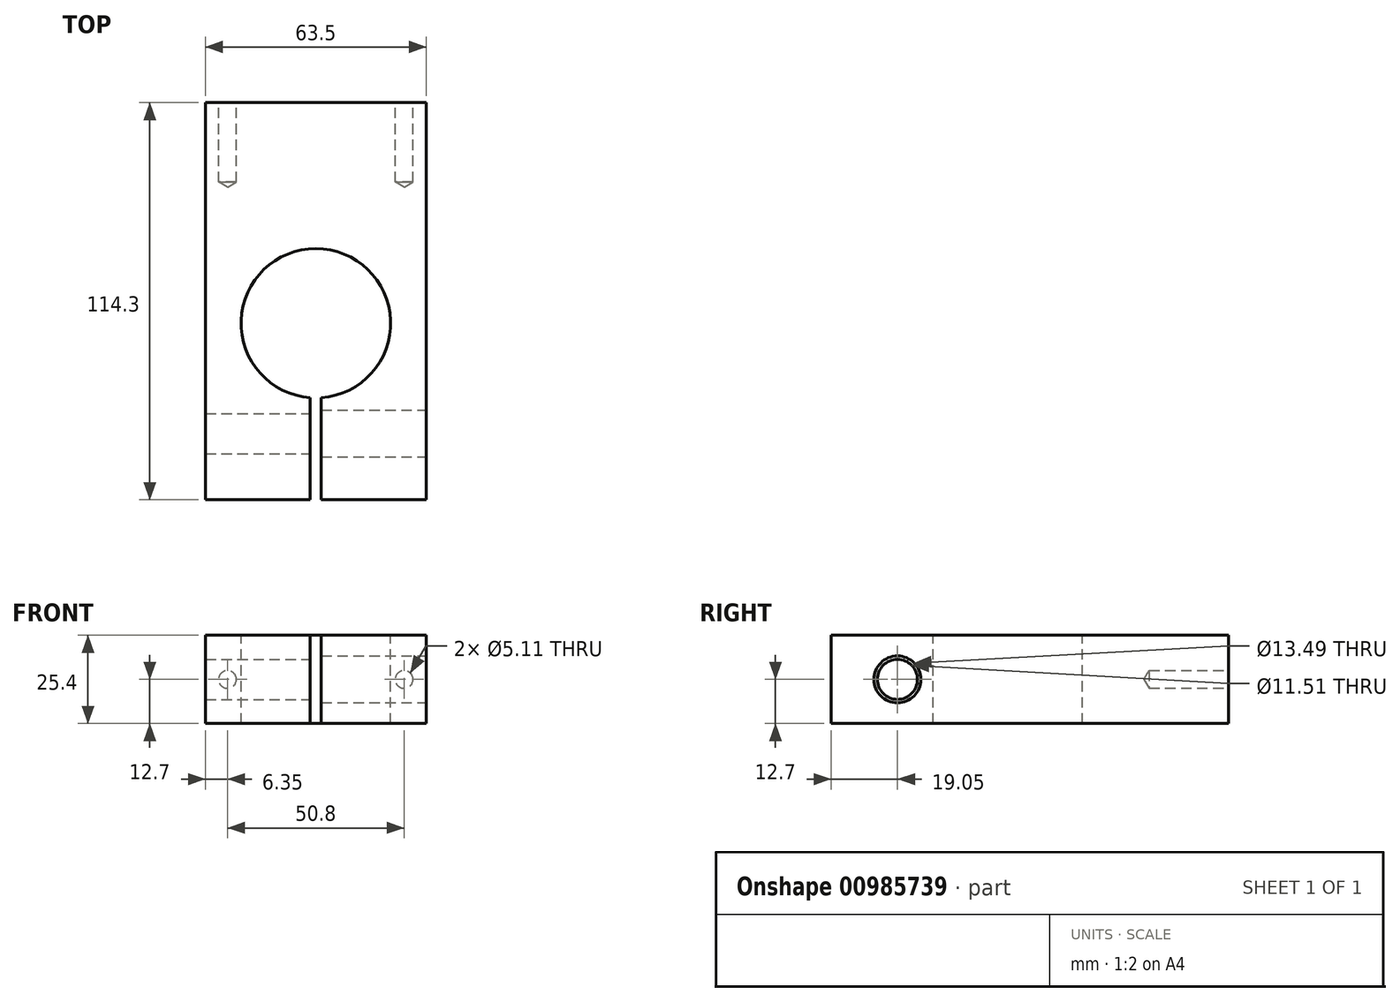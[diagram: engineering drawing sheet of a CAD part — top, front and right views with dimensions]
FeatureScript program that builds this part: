
annotation { "Feature Type Name" : "Feature", "Feature Type Description" : "" }
export const myFeature = defineFeature(function(context is Context, id is Id, definition is map)
    precondition{}
    {
        {
            var Q0;
            Q0=qCreatedBy(makeId("Top.planeOp"),FACE);
            var sketch = newSketch(context, id + "F0", { "sketchPlane" : qUnion([Q0])});
            skLineSegment(sketch, "E0.bottom", {"start": v(0, 0) * mm, "end": v(63.5, 0) * mm});
            skLineSegment(sketch, "E0.top", {"start": v(0, -114.3) * mm, "end": v(63.5, -114.3) * mm});
            skLineSegment(sketch, "E0.left", {"start": v(0, 0) * mm, "end": v(0, -114.3) * mm});
            skLineSegment(sketch, "E0.right", {"start": v(63.5, 0) * mm, "end": v(63.5, -114.3) * mm});
            skSolve(sketch);
        }
        {
            var Q0;
            Q0 = qSketchRegion(id + "F0", true);
            extrude(context, id + "F1", {"entities" : qUnion([Q0]), "depth" : 25.4 * mm, "offsetDistance" : 25.4 * mm});
        }
        {
            var Q0;
            Q0=makeQuery(id+"F1.opExtrude","SWEPT_FACE",FACE,{"disambiguationData":[OSD([sQuery(id+"F0.wireOp",EDGE,"E0.bottom")])]});
            var sketch = newSketch(context, id + "F2", { "sketchPlane" : qUnion([Q0])});
            skLineSegment(sketch, "E1", {"start": v(-57.15, 12.7) * mm, "end": v(-6.35, 12.7) * mm, "construction": true});
            skLineSegment(sketch, "E2", {"start": v(-57.15, 12.7) * mm, "end": v(-63.5, 12.7) * mm, "construction": true});
            skLineSegment(sketch, "E3", {"start": v(-31.75, 12.7) * mm, "end": v(-31.75, 25.4) * mm, "construction": true});
            skSolve(sketch);
        }
        {
            var Q0;
            Q0=sQuery(id+"F2.wireOp",VERTEX,"E1.start");
            var Q1;
            Q1=sQuery(id+"F2.wireOp",VERTEX,"E1.end");
            var Q2;
            Q2=makeQuery(id+"F1.opExtrude","SWEPT_BODY",BODY,{"disambiguationData":[OSD([sQuery(id+"F0.wireOp",EDGE,"E0.bottom"),sQuery(id+"F0.wireOp",EDGE,"E0.top"),sQuery(id+"F0.wireOp",EDGE,"E0.left"),sQuery(id+"F0.wireOp",EDGE,"E0.right")])]});
            hole(context, id + "F3", {"style" : HoleStyle.SIMPLE, "endStyle" : HoleEndStyle.BLIND, "standardTappedOrClearance" : lookupTablePath({ "standard" : "ANSI", "engagement" : "75%", "pitch" : "20 tpi", "size" : "1/4", "type" : "Tapped" }), "standardBlindInLast" : lookupTablePath({ "standard" : "ANSI", "fit" : "Free", "engagement" : "75%", "pitch" : "20 tpi", "size" : "1/4", "type" : "Clearance & tapped" }), "holeDiameter" : 5.1 * mm, "majorDiameter" : 6.35 * mm, "showTappedDepth" : true, "holeDepth" : 22.86 * mm, "isTappedThrough" : true, "tappedDepth" : 19.05 * mm, "tapClearance" : 3, "startFromSketch" : true, "locations" : qUnion([Q0, Q1]), "scope" : qUnion([Q2])});
        }
        {
            var Q0;
            Q0=makeQuery(id+"F1.opExtrude","CAP_FACE",FACE,{"disambiguationData":[OSD([sQuery(id+"F0.wireOp",EDGE,"E0.bottom"),sQuery(id+"F0.wireOp",EDGE,"E0.top"),sQuery(id+"F0.wireOp",EDGE,"E0.left"),sQuery(id+"F0.wireOp",EDGE,"E0.right")])],"isStart":false});
            var sketch = newSketch(context, id + "F4", { "sketchPlane" : qUnion([Q0])});
            skArc(sketch, "E4", {"start": v(33.34, -84.94) * mm, "mid": v(31.75, -42) * mm, "end": v(30.16, -84.94) * mm});
            skPoint(sketch, "E4.centerSnap0", {"position": v(31.75, -114.3) * mm});
            skLineSegment(sketch, "E5", {"start": v(31.75, -63.5) * mm, "end": v(31.75, 0) * mm, "construction": true});
            skLineSegment(sketch, "E6.top", {"start": v(30.16, -114.3) * mm, "end": v(33.34, -114.3) * mm});
            skLineSegment(sketch, "E6.left", {"start": v(30.16, -84.94) * mm, "end": v(30.16, -114.3) * mm});
            skLineSegment(sketch, "E6.right", {"start": v(33.34, -84.94) * mm, "end": v(33.34, -114.3) * mm});
            skLineSegment(sketch, "E7", {"start": v(30.16, -84.94) * mm, "end": v(33.34, -84.94) * mm, "construction": true});
            skSolve(sketch);
        }
        {
            var Q0;
            Q0 = qSketchRegion(id + "F4", true);
            extrude(context, id + "F5", {"entities" : qUnion([Q0]), "operationType" : NewBodyOperationType.REMOVE, "endBound" : BoundingType.UP_TO_NEXT, "oppositeDirection" : true, "depth" : 25.4 * mm, "offsetDistance" : 25.4 * mm});
        }
        {
            var Q0;
            Q0=makeQuery(id+"F1.opExtrude","SWEPT_FACE",FACE,{"disambiguationData":[OSD([sQuery(id+"F0.wireOp",EDGE,"E0.right")])]});
            var sketch = newSketch(context, id + "F6", { "sketchPlane" : qUnion([Q0])});
            skLineSegment(sketch, "E8", {"start": v(-114.3, 12.7) * mm, "end": v(-95.25, 12.7) * mm, "construction": true});
            skLineSegment(sketch, "E9", {"start": v(-63.5, 25.4) * mm, "end": v(-63.5, 0) * mm, "construction": true});
            skCircle(sketch, "E10", {"center": v(-95.25, 12.7) * mm, "radius": 6.75 * mm});
            skSolve(sketch);
        }
        {
            var Q0;
            Q0 = qSketchRegion(id + "F6", true);
            extrude(context, id + "F7", {"entities" : qUnion([Q0]), "operationType" : NewBodyOperationType.REMOVE, "endBound" : BoundingType.UP_TO_NEXT, "oppositeDirection" : true, "depth" : 25.4 * mm, "offsetDistance" : 25.4 * mm});
        }
        {
            var Q0;
            Q0=makeQuery(id+"F5.boolean.opBoolean","COPY",FACE,{"derivedFrom":makeQuery(id+"F5.opExtrude","SWEPT_FACE",FACE,{"disambiguationData":[OSD([sQuery(id+"F4.wireOp",EDGE,"E6.left")])]})});
            var sketch = newSketch(context, id + "F8", { "sketchPlane" : qUnion([Q0])});
            skCircle(sketch, "E11.0", {"center": v(-95.25, 12.7) * mm, "radius": 6.75 * mm});
            skSolve(sketch);
        }
        {
            var Q0;
            Q0=sQuery(id+"F8.wireOp",VERTEX,"E11.0.center");
            var Q1;
            Q1=makeQuery(id+"F1.opExtrude","SWEPT_BODY",BODY,{"disambiguationData":[OSD([sQuery(id+"F0.wireOp",EDGE,"E0.bottom"),sQuery(id+"F0.wireOp",EDGE,"E0.top"),sQuery(id+"F0.wireOp",EDGE,"E0.left"),sQuery(id+"F0.wireOp",EDGE,"E0.right")])]});
            hole(context, id + "F9", {"style" : HoleStyle.SIMPLE, "endStyle" : HoleEndStyle.THROUGH, "standardTappedOrClearance" : lookupTablePath({ "standard" : "ANSI", "engagement" : "75%", "pitch" : "20 tpi", "size" : "1/2", "type" : "Tapped" }), "standardBlindInLast" : lookupTablePath({ "standard" : "ANSI", "fit" : "Free", "engagement" : "75%", "pitch" : "20 tpi", "size" : "1/2", "type" : "Clearance & tapped" }), "holeDiameter" : 11.5 * mm, "majorDiameter" : 12.7 * mm, "showTappedDepth" : true, "isTappedThrough" : true, "tappedDepth" : 19.05 * mm, "tapClearance" : 3, "startFromSketch" : true, "locations" : qUnion([Q0]), "scope" : qUnion([Q1])});
        }
    });
